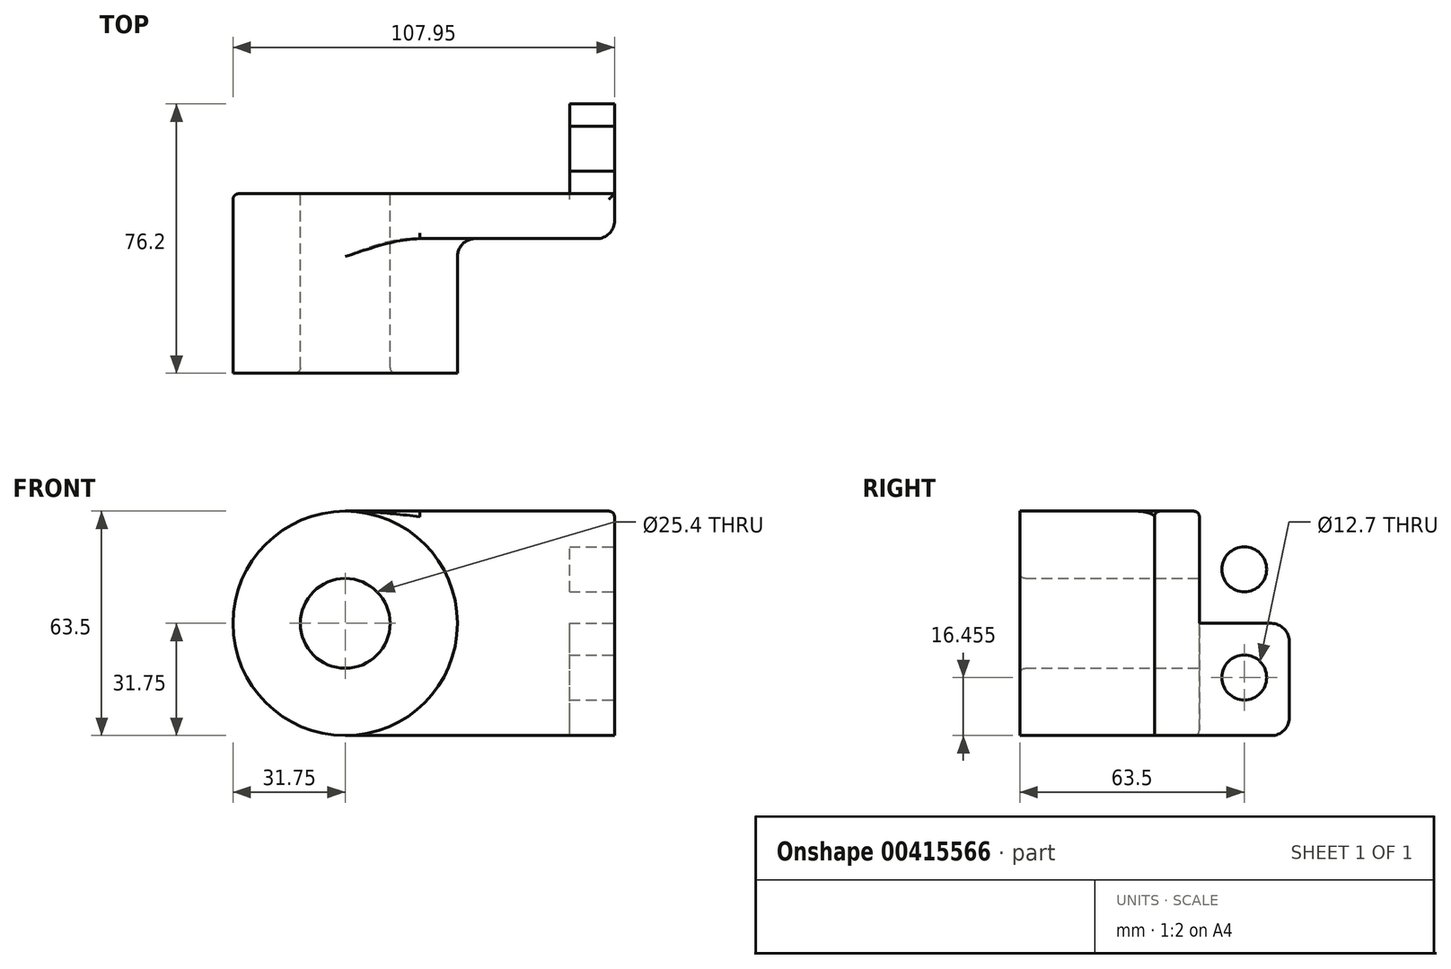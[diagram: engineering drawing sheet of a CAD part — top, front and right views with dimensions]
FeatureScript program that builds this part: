
annotation { "Feature Type Name" : "Feature", "Feature Type Description" : "" }
export const myFeature = defineFeature(function(context is Context, id is Id, definition is map)
    precondition{}
    {
        {
            var Q0;
            Q0=qCreatedBy(makeId("Front.planeOp"),FACE);
            var sketch = newSketch(context, id + "F0", { "sketchPlane" : qUnion([Q0])});
            skLineSegment(sketch, "E0.bottom", {"start": v(38.1, -31.75) * mm, "end": v(-38.1, -31.75) * mm});
            skLineSegment(sketch, "E0.top", {"start": v(38.1, 31.75) * mm, "end": v(-38.1, 31.75) * mm});
            skLineSegment(sketch, "E0.left", {"start": v(38.1, -31.75) * mm, "end": v(38.1, 31.75) * mm});
            skLineSegment(sketch, "E0.right", {"start": v(-38.1, -31.75) * mm, "end": v(-38.1, 31.75) * mm});
            skPoint(sketch, "E0.middle", {"position": v(0, 0) * mm});
            skCircle(sketch, "E1", {"center": v(-38.1, 0) * mm, "radius": 31.75 * mm});
            skCircle(sketch, "E2", {"center": v(-38.1, 0) * mm, "radius": 12.7 * mm});
            skSolve(sketch);
        }
        {
            var Q0;
            {var subQ0=sQuery(id+"F0.wireOp",EDGE,"E0.bottom");Q0=makeQuery(id+"F0.imprint","IMPRINT",FACE,{"disambiguationData":[TD([[makeQuery(id+"F0.imprint","IMPRINT",EDGE,{"derivedFrom":subQ0}),-1.0]])]});}
            var Q1;
            {var subQ1=sQuery(id+"F0.wireOp",EDGE,"E0.right");var subQ3=sQuery(id+"F0.wireOp",EDGE,"E2");var subQ4=makeQuery(id+"F0.imprint","INTERSECT",VERTEX,{"disambiguationData":[OD(0.0)],"derivedFrom":[subQ1,subQ3]});Q1=makeQuery(id+"F0.imprint","IMPRINT",FACE,{"disambiguationData":[TD([[makeQuery(id+"F0.imprint","IMPRINT",EDGE,{"disambiguationData":[TD([[subQ4,1.0]])],"derivedFrom":subQ3}),-1.0]])]});}
            var Q2;
            {var subQ1=sQuery(id+"F0.wireOp",EDGE,"E0.right");var subQ3=sQuery(id+"F0.wireOp",EDGE,"E2");var subQ4=makeQuery(id+"F0.imprint","INTERSECT",VERTEX,{"disambiguationData":[OD(0.0)],"derivedFrom":[subQ1,subQ3]});Q2=makeQuery(id+"F0.imprint","IMPRINT",FACE,{"disambiguationData":[TD([[makeQuery(id+"F0.imprint","IMPRINT",EDGE,{"disambiguationData":[TD([[subQ4,-1.0]])],"derivedFrom":subQ3}),-1.0]])]});}
            extrude(context, id + "F1", {"entities" : qUnion([Q0, Q1, Q2]), "depth" : 12.7 * mm});
        }
        {
            var Q0;
            {var subQ1=sQuery(id+"F0.wireOp",EDGE,"E0.right");var subQ3=sQuery(id+"F0.wireOp",EDGE,"E2");var subQ4=makeQuery(id+"F0.imprint","INTERSECT",VERTEX,{"disambiguationData":[OD(0.0)],"derivedFrom":[subQ1,subQ3]});Q0=makeQuery(id+"F0.imprint","IMPRINT",FACE,{"disambiguationData":[TD([[makeQuery(id+"F0.imprint","IMPRINT",EDGE,{"disambiguationData":[TD([[subQ4,-1.0]])],"derivedFrom":subQ3}),-1.0]])]});}
            var Q1;
            {var subQ1=sQuery(id+"F0.wireOp",EDGE,"E0.right");var subQ3=sQuery(id+"F0.wireOp",EDGE,"E2");var subQ4=makeQuery(id+"F0.imprint","INTERSECT",VERTEX,{"disambiguationData":[OD(0.0)],"derivedFrom":[subQ1,subQ3]});Q1=makeQuery(id+"F0.imprint","IMPRINT",FACE,{"disambiguationData":[TD([[makeQuery(id+"F0.imprint","IMPRINT",EDGE,{"disambiguationData":[TD([[subQ4,1.0]])],"derivedFrom":subQ3}),-1.0]])]});}
            var Q2;
            Q2=sQuery(id+"F0.wireOp",EDGE,"E1");
            extrude(context, id + "F2", {"entities" : qUnion([Q0, Q1]), "operationType" : NewBodyOperationType.ADD, "surfaceEntities" : qUnion([Q2]), "depth" : 50.8 * mm});
        }
        {
            var Q0;
            Q0=makeQuery(id+"F1.opExtrude","SWEPT_FACE",FACE,{"disambiguationData":[OSD([sQuery(id+"F0.wireOp",EDGE,"E0.left")])]});
            var sketch = newSketch(context, id + "F3", { "sketchPlane" : qUnion([Q0])});
            skLineSegment(sketch, "E3.bottom", {"start": v(-12.7, -31.75) * mm, "end": v(25.4, -31.75) * mm});
            skLineSegment(sketch, "E3.top", {"start": v(-12.7, 31.75) * mm, "end": v(25.4, 31.75) * mm});
            skLineSegment(sketch, "E3.left", {"start": v(-12.7, -31.75) * mm, "end": v(-12.7, 31.75) * mm});
            skLineSegment(sketch, "E3.right", {"start": v(25.4, -31.75) * mm, "end": v(25.4, 31.75) * mm});
            skCircle(sketch, "E4", {"center": v(12.7, -15.3) * mm, "radius": 6.35 * mm});
            skLineSegment(sketch, "E5", {"start": v(-12.7, 0) * mm, "end": v(25.4, 0) * mm});
            skCircle(sketch, "E6.MirrorC", {"center": v(12.7, 15.3) * mm, "radius": 6.35 * mm});
            skSolve(sketch);
        }
        {
            var Q0;
            Q0=makeQuery(id+"F3.imprint","IMPRINT",FACE,{"disambiguationData":[TD([[makeQuery(id+"F3.imprint","IMPRINT",EDGE,{"derivedFrom":sQuery(id+"F3.wireOp",EDGE,"E4")}),-1.0]])]});
            var Q1;
            Q1=makeQuery(id+"F3.imprint","IMPRINT",FACE,{"disambiguationData":[TD([[makeQuery(id+"F3.imprint","IMPRINT",EDGE,{"derivedFrom":sQuery(id+"F3.wireOp",EDGE,"E6.MirrorC")}),1.0]])]});
            var Q2;
            {var subQ0=sQuery(id+"F3.wireOp",EDGE,"E3.top");var subQ1=makeQuery(id+"F1.opExtrude","CAP_EDGE",EDGE,{"disambiguationData":[OSD([sQuery(id+"F0.wireOp",EDGE,"E0.left")])],"isStart":true});var subQ2=makeQuery(id+"F3.imprint","INTERSECT",VERTEX,{"derivedFrom":[subQ1,subQ0]});Q2=makeQuery(id+"F3.imprint","IMPRINT",FACE,{"disambiguationData":[TD([[makeQuery(id+"F3.imprint","IMPRINT",EDGE,{"disambiguationData":[TD([[subQ2,1.0]])],"derivedFrom":subQ0}),-1.0]])]});}
            var Q3;
            {var subQ0=sQuery(id+"F3.wireOp",EDGE,"E3.bottom");var subQ1=makeQuery(id+"F1.opExtrude","CAP_EDGE",EDGE,{"disambiguationData":[OSD([sQuery(id+"F0.wireOp",EDGE,"E0.left")])],"isStart":true});var subQ2=makeQuery(id+"F3.imprint","INTERSECT",VERTEX,{"derivedFrom":[subQ1,subQ0]});Q3=makeQuery(id+"F3.imprint","IMPRINT",FACE,{"disambiguationData":[TD([[makeQuery(id+"F3.imprint","IMPRINT",EDGE,{"disambiguationData":[TD([[subQ2,1.0]])],"derivedFrom":subQ0}),1.0]])]});}
            extrude(context, id + "F4", {"entities" : qUnion([Q0, Q1, Q2, Q3]), "operationType" : NewBodyOperationType.ADD, "oppositeDirection" : true, "depth" : 12.7 * mm});
        }
        {
            var Q0;
            {var subQ0=sQuery(id+"F0.wireOp",EDGE,"E1");Q0=makeQuery(id+"F2.boolean.opBoolean","INTERSECT",EDGE,{"derivedFrom":[makeQuery(id+"F1.opExtrude","CAP_FACE",FACE,{"disambiguationData":[OSD([sQuery(id+"F0.wireOp",EDGE,"E0.bottom"),sQuery(id+"F0.wireOp",EDGE,"E0.top"),sQuery(id+"F0.wireOp",EDGE,"E0.left"),subQ0,sQuery(id+"F0.wireOp",EDGE,"E2")])],"isStart":false}),makeQuery(id+"F2.opExtrude","SWEPT_FACE",FACE,{"disambiguationData":[OSD([subQ0])]})]});}
            var Q1;
            Q1=makeQuery(id+"F1.opExtrude","CAP_EDGE",EDGE,{"disambiguationData":[OSD([sQuery(id+"F0.wireOp",EDGE,"E0.left")])],"isStart":false});
            var Q2;
            Q2=makeQuery(id+"F4.opExtrude","SWEPT_EDGE",EDGE,{"disambiguationData":[OSD([sQuery(id+"F3.wireOp",EDGE,"E3.bottom"),sQuery(id+"F3.wireOp",EDGE,"E3.right")])]});
            var Q3;
            Q3=makeQuery(id+"F4.opExtrude","SWEPT_EDGE",EDGE,{"disambiguationData":[OSD([sQuery(id+"F3.wireOp",EDGE,"E3.top"),sQuery(id+"F3.wireOp",EDGE,"E3.right")])]});
            fillet(context, id + "F5", {"entities" : qUnion([Q0, Q1, Q2, Q3]), "radius" : 5.08 * mm, "tangentPropagation" : true, "allowEdgeOverflow" : false});
        }
        {
            var Q0;
            Q0=makeQuery(id+"F1.opExtrude","CAP_EDGE",EDGE,{"disambiguationData":[OSD([sQuery(id+"F0.wireOp",EDGE,"E0.top")])],"isStart":false});
            var Q1;
            Q1=makeQuery(id+"F1.opExtrude","CAP_EDGE",EDGE,{"disambiguationData":[OSD([sQuery(id+"F0.wireOp",EDGE,"E0.top")])],"isStart":true});
            var Q2;
            Q2=makeQuery(id+"F4.opExtrude","CAP_EDGE",EDGE,{"disambiguationData":[OSD([sQuery(id+"F3.wireOp",EDGE,"E3.top")])],"isStart":false});
            var Q3;
            Q3=makeQuery(id+"F2.opExtrude","CAP_EDGE",EDGE,{"disambiguationData":[OSD([sQuery(id+"F0.wireOp",EDGE,"E2")])],"isStart":false});
            fillet(context, id + "F6", {"entities" : qUnion([Q0, Q1, Q2, Q3]), "radius" : 1.59 * mm, "tangentPropagation" : true, "allowEdgeOverflow" : false});
        }
    });
